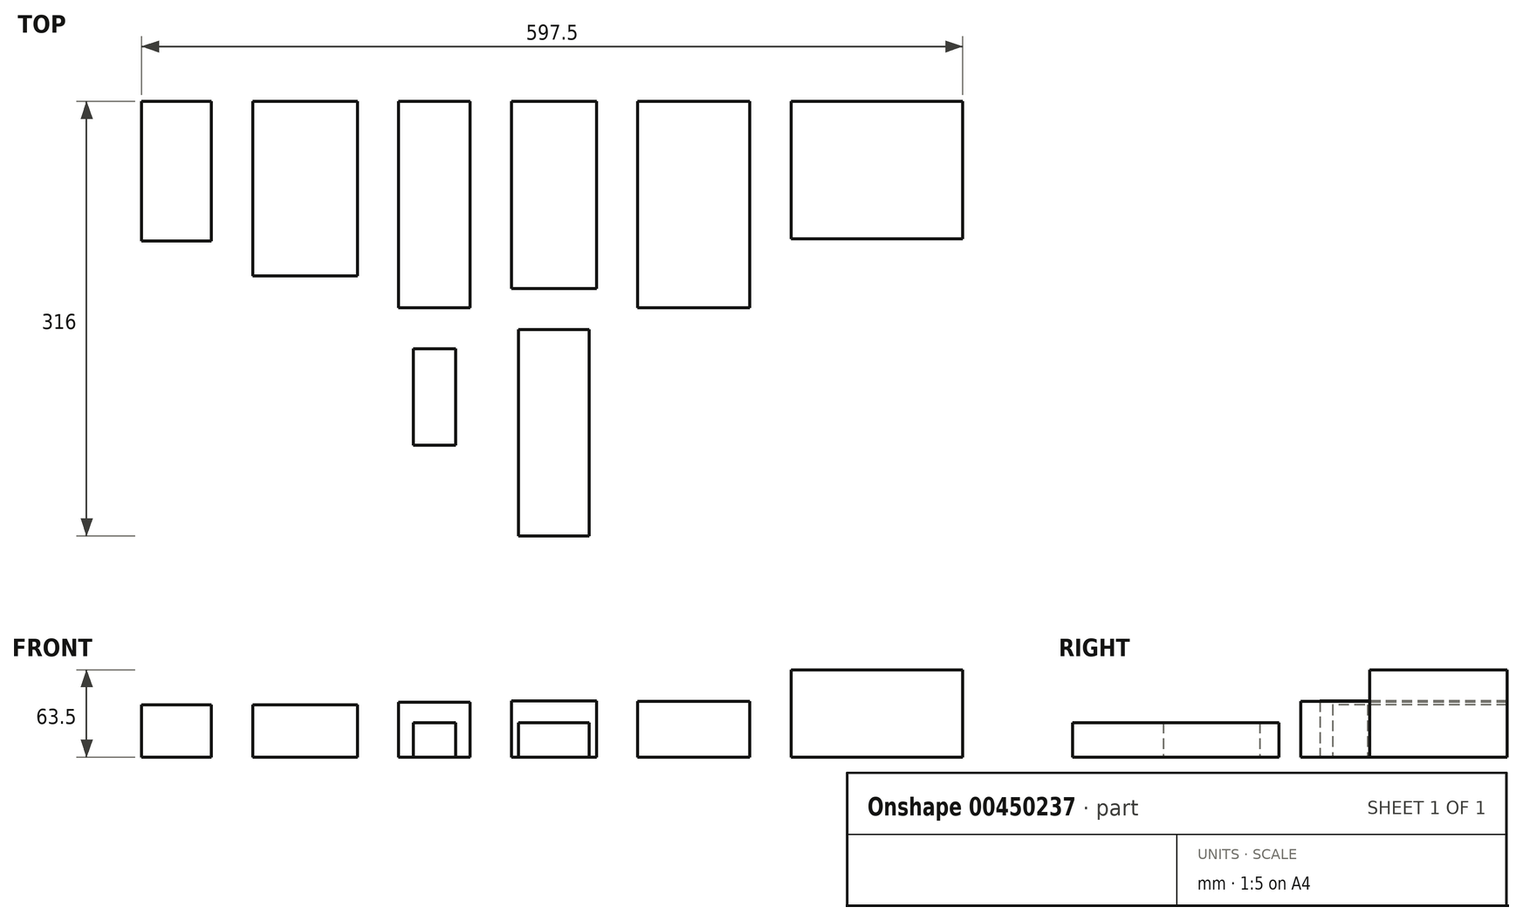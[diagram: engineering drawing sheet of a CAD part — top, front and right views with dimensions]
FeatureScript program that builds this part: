
annotation { "Feature Type Name" : "Feature", "Feature Type Description" : "" }
export const myFeature = defineFeature(function(context is Context, id is Id, definition is map)
    precondition{}
    {
        {
            var Q0;
            Q0=qCreatedBy(makeId("Top.planeOp"),FACE);
            var sketch = newSketch(context, id + "F0", { "sketchPlane" : qUnion([Q0])});
            skLineSegment(sketch, "E0.bottom", {"start": v(-137.23, 104.15) * mm, "end": v(-86.43, 104.15) * mm});
            skLineSegment(sketch, "E0.top", {"start": v(-137.23, 2.55) * mm, "end": v(-86.43, 2.55) * mm});
            skLineSegment(sketch, "E0.left", {"start": v(-137.23, 104.15) * mm, "end": v(-137.23, 2.55) * mm});
            skLineSegment(sketch, "E0.right", {"start": v(-86.43, 104.15) * mm, "end": v(-86.43, 2.55) * mm});
            skLineSegment(sketch, "E1", {"start": v(-86.43, 104.15) * mm, "end": v(-56.43, 104.15) * mm, "construction": true});
            skLineSegment(sketch, "E2.bottom", {"start": v(-56.43, 104.15) * mm, "end": v(19.77, 104.15) * mm});
            skLineSegment(sketch, "E2.top", {"start": v(-56.43, -22.85) * mm, "end": v(19.77, -22.85) * mm});
            skLineSegment(sketch, "E2.left", {"start": v(-56.43, 104.15) * mm, "end": v(-56.43, -22.85) * mm});
            skLineSegment(sketch, "E2.right", {"start": v(19.77, 104.15) * mm, "end": v(19.77, -22.85) * mm});
            skLineSegment(sketch, "E3", {"start": v(19.77, 104.15) * mm, "end": v(49.77, 104.15) * mm, "construction": true});
            skLineSegment(sketch, "E4.bottom", {"start": v(49.77, 104.15) * mm, "end": v(101.77, 104.15) * mm});
            skLineSegment(sketch, "E4.top", {"start": v(49.77, -45.85) * mm, "end": v(101.77, -45.85) * mm});
            skLineSegment(sketch, "E4.left", {"start": v(49.77, 104.15) * mm, "end": v(49.77, -45.85) * mm});
            skLineSegment(sketch, "E4.right", {"start": v(101.77, 104.15) * mm, "end": v(101.77, -45.85) * mm});
            skLineSegment(sketch, "E5.bottom", {"start": v(223.77, 104.15) * mm, "end": v(305.27, 104.15) * mm});
            skLineSegment(sketch, "E5.top", {"start": v(223.77, -45.85) * mm, "end": v(305.27, -45.85) * mm});
            skLineSegment(sketch, "E5.left", {"start": v(223.77, 104.15) * mm, "end": v(223.77, -45.85) * mm});
            skLineSegment(sketch, "E5.right", {"start": v(305.27, 104.15) * mm, "end": v(305.27, -45.85) * mm});
            skLineSegment(sketch, "E6", {"start": v(305.27, 104.15) * mm, "end": v(335.27, 104.15) * mm, "construction": true});
            skLineSegment(sketch, "E7.bottom", {"start": v(335.27, 104.15) * mm, "end": v(460.27, 104.15) * mm});
            skLineSegment(sketch, "E7.top", {"start": v(335.27, 4.15) * mm, "end": v(460.27, 4.15) * mm});
            skLineSegment(sketch, "E7.left", {"start": v(335.27, 104.15) * mm, "end": v(335.27, 4.15) * mm});
            skLineSegment(sketch, "E7.right", {"start": v(460.27, 104.15) * mm, "end": v(460.27, 4.15) * mm});
            skLineSegment(sketch, "E8", {"start": v(60.27, -75.85) * mm, "end": v(91.27, -75.85) * mm});
            skLineSegment(sketch, "E9", {"start": v(75.77, -45.85) * mm, "end": v(75.77, -75.85) * mm, "construction": true});
            skLineSegment(sketch, "E10", {"start": v(60.27, -75.85) * mm, "end": v(60.27, -145.85) * mm});
            skLineSegment(sketch, "E11", {"start": v(60.27, -145.85) * mm, "end": v(91.27, -145.85) * mm});
            skLineSegment(sketch, "E12", {"start": v(91.27, -145.85) * mm, "end": v(91.27, -75.85) * mm});
            skLineSegment(sketch, "E13", {"start": v(101.77, 104.15) * mm, "end": v(131.77, 104.15) * mm, "construction": true});
            skLineSegment(sketch, "E14.bottom", {"start": v(131.77, 104.15) * mm, "end": v(193.77, 104.15) * mm});
            skLineSegment(sketch, "E14.top", {"start": v(131.77, -31.85) * mm, "end": v(193.77, -31.85) * mm});
            skLineSegment(sketch, "E14.left", {"start": v(131.77, 104.15) * mm, "end": v(131.77, -31.85) * mm});
            skLineSegment(sketch, "E14.right", {"start": v(193.77, 104.15) * mm, "end": v(193.77, -31.85) * mm});
            skLineSegment(sketch, "E15", {"start": v(193.77, 104.15) * mm, "end": v(223.77, 104.15) * mm, "construction": true});
            skLineSegment(sketch, "E16.bottom", {"start": v(137.02, -61.85) * mm, "end": v(188.52, -61.85) * mm});
            skLineSegment(sketch, "E16.top", {"start": v(137.02, -211.85) * mm, "end": v(188.52, -211.85) * mm});
            skLineSegment(sketch, "E16.left", {"start": v(137.02, -61.85) * mm, "end": v(137.02, -211.85) * mm});
            skLineSegment(sketch, "E16.right", {"start": v(188.52, -61.85) * mm, "end": v(188.52, -211.85) * mm});
            skLineSegment(sketch, "E17", {"start": v(162.77, -31.85) * mm, "end": v(162.77, -61.85) * mm, "construction": true});
            skSolve(sketch);
        }
        {
            var Q0;
            Q0=makeQuery(id+"F0.imprint","IMPRINT",FACE,{"disambiguationData":[TD([[makeQuery(id+"F0.imprint","IMPRINT",EDGE,{"derivedFrom":sQuery(id+"F0.wireOp",EDGE,"E0.bottom")}),-1.0]])]});
            var Q1;
            Q1=makeQuery(id+"F0.imprint","IMPRINT",FACE,{"disambiguationData":[TD([[makeQuery(id+"F0.imprint","IMPRINT",EDGE,{"derivedFrom":sQuery(id+"F0.wireOp",EDGE,"E2.bottom")}),-1.0]])]});
            extrude(context, id + "F1", {"entities" : qUnion([Q0, Q1]), "depth" : 38 * mm});
        }
        {
            var Q0;
            Q0=makeQuery(id+"F0.imprint","IMPRINT",FACE,{"disambiguationData":[TD([[makeQuery(id+"F0.imprint","IMPRINT",EDGE,{"derivedFrom":sQuery(id+"F0.wireOp",EDGE,"E4.bottom")}),-1.0]])]});
            extrude(context, id + "F2", {"entities" : qUnion([Q0]), "depth" : 40 * mm});
        }
        {
            var Q0;
            Q0=makeQuery(id+"F0.imprint","IMPRINT",FACE,{"disambiguationData":[TD([[makeQuery(id+"F0.imprint","IMPRINT",EDGE,{"derivedFrom":sQuery(id+"F0.wireOp",EDGE,"E5.bottom")}),-1.0]])]});
            extrude(context, id + "F3", {"entities" : qUnion([Q0]), "depth" : 40.5 * mm});
        }
        {
            var Q0;
            Q0=makeQuery(id+"F0.imprint","IMPRINT",FACE,{"disambiguationData":[TD([[makeQuery(id+"F0.imprint","IMPRINT",EDGE,{"derivedFrom":sQuery(id+"F0.wireOp",EDGE,"E7.bottom")}),-1.0]])]});
            extrude(context, id + "F4", {"entities" : qUnion([Q0]), "depth" : 63.5 * mm});
        }
        {
            var Q0;
            Q0=makeQuery(id+"F0.imprint","IMPRINT",FACE,{"disambiguationData":[TD([[makeQuery(id+"F0.imprint","IMPRINT",EDGE,{"derivedFrom":sQuery(id+"F0.wireOp",EDGE,"E8")}),-1.0]])]});
            extrude(context, id + "F5", {"entities" : qUnion([Q0]), "depth" : 25 * mm});
        }
        {
            var Q0;
            Q0=makeQuery(id+"F0.imprint","IMPRINT",FACE,{"disambiguationData":[TD([[makeQuery(id+"F0.imprint","IMPRINT",EDGE,{"derivedFrom":sQuery(id+"F0.wireOp",EDGE,"E14.bottom")}),-1.0]])]});
            extrude(context, id + "F6", {"entities" : qUnion([Q0]), "depth" : 41 * mm});
        }
        {
            var Q0;
            Q0=makeQuery(id+"F0.imprint","IMPRINT",FACE,{"disambiguationData":[TD([[makeQuery(id+"F0.imprint","IMPRINT",EDGE,{"derivedFrom":sQuery(id+"F0.wireOp",EDGE,"E16.bottom")}),-1.0]])]});
            extrude(context, id + "F7", {"entities" : qUnion([Q0]), "depth" : 25 * mm});
        }
    });
